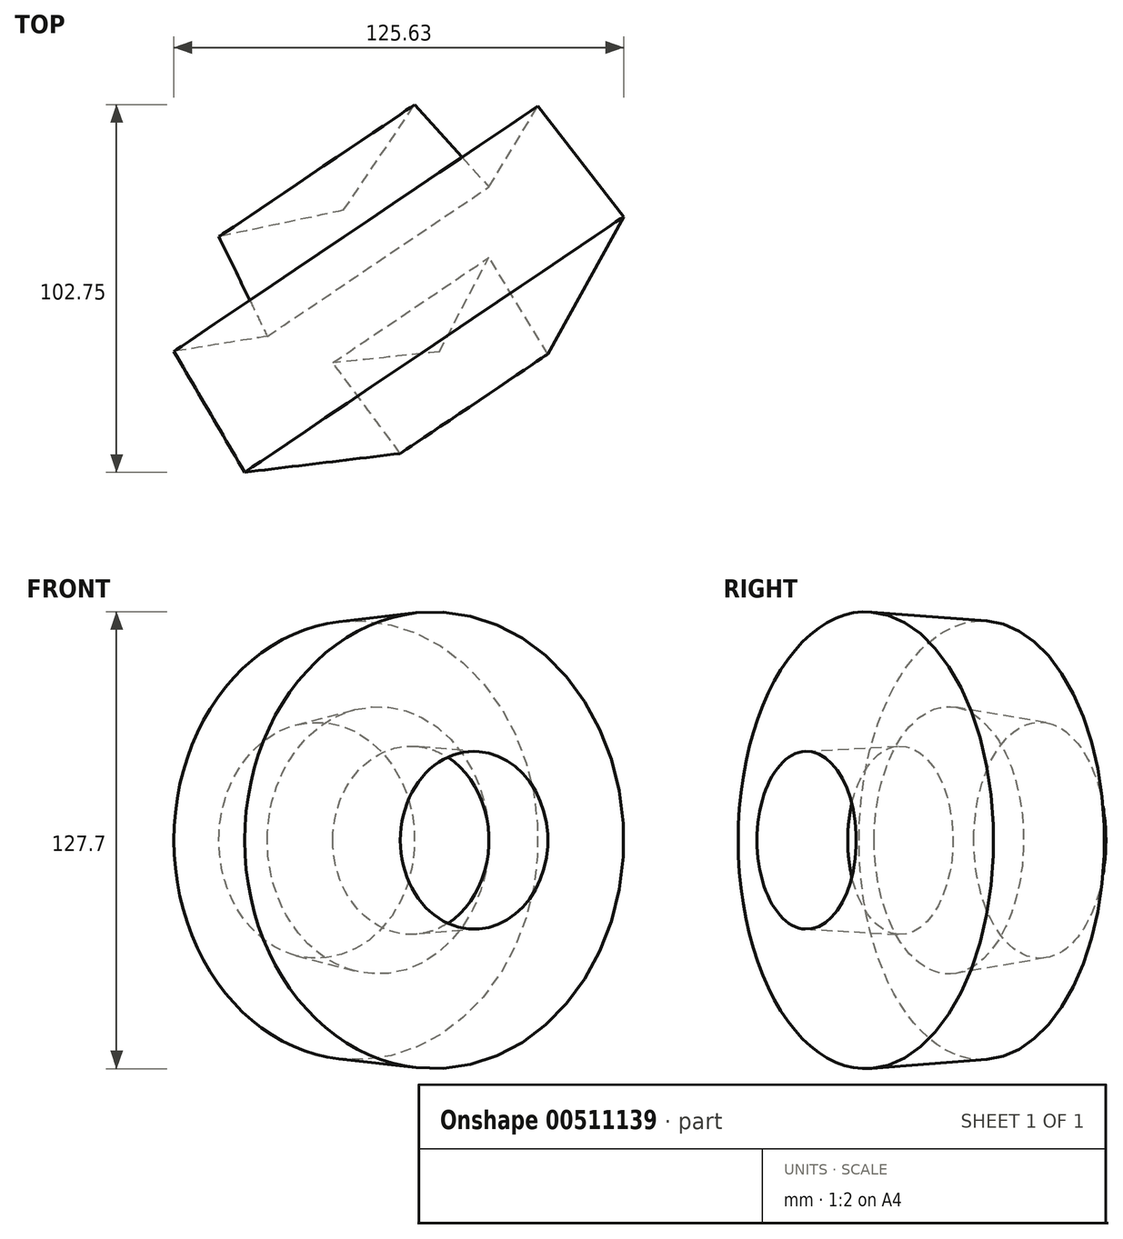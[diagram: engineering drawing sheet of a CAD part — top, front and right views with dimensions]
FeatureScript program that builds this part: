
annotation { "Feature Type Name" : "Feature", "Feature Type Description" : "" }
export const myFeature = defineFeature(function(context is Context, id is Id, definition is map)
    precondition{}
    {
        {
            var Q0;
            Q0=qCreatedBy(makeId("Top.planeOp"),FACE);
            var sketch = newSketch(context, id + "F0", { "sketchPlane" : qUnion([Q0])});
            skLineSegment(sketch, "E0", {"start": v(-40.64, 28) * mm, "end": v(-13.94, -11.58) * mm});
            skLineSegment(sketch, "E1", {"start": v(-13.94, -11.58) * mm, "end": v(0, 14.81) * mm});
            skLineSegment(sketch, "E2", {"start": v(0, 14.81) * mm, "end": v(16.44, -12.2) * mm});
            skLineSegment(sketch, "E3", {"start": v(16.44, -12.2) * mm, "end": v(37.61, 26.17) * mm});
            skLineSegment(sketch, "E4", {"start": v(37.61, 26.17) * mm, "end": v(13.68, 57.16) * mm});
            skLineSegment(sketch, "E5", {"start": v(13.68, 57.16) * mm, "end": v(0, 34.54) * mm});
            skLineSegment(sketch, "E6", {"start": v(0, 34.54) * mm, "end": v(-20.75, 57.52) * mm});
            skLineSegment(sketch, "E7", {"start": v(-20.75, 57.52) * mm, "end": v(-40.64, 28) * mm});
            skSolve(sketch);
        }
        {
            var Q0;
            Q0=makeQuery(id+"F0.imprint","IMPRINT",FACE,{"disambiguationData":[TD([[makeQuery(id+"F0.imprint","IMPRINT",EDGE,{"derivedFrom":sQuery(id+"F0.wireOp",EDGE,"E0")}),1.0]])]});
            var Q1;
            Q1=sQuery(id+"F0.wireOp",EDGE,"E0");
            revolve(context, id + "F1", {"entities" : qUnion([Q0]), "axis" : qUnion([Q1]), "revolveType" : RevolveType.FULL});
        }
    });
